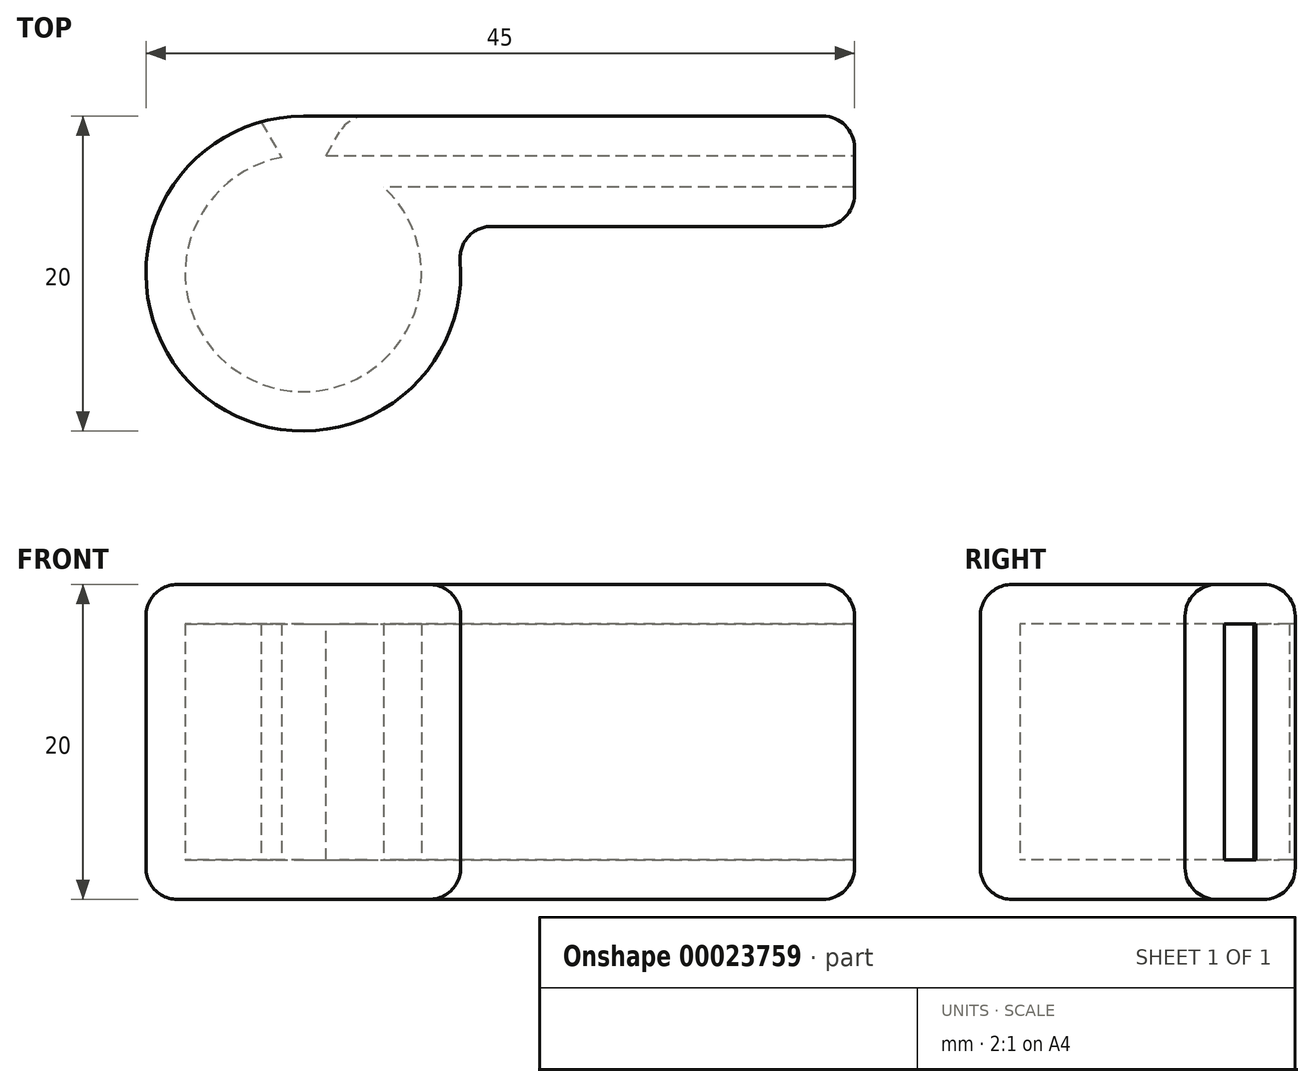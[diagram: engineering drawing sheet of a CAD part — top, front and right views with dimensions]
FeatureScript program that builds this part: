
annotation { "Feature Type Name" : "Feature", "Feature Type Description" : "" }
export const myFeature = defineFeature(function(context is Context, id is Id, definition is map)
    precondition{}
    {
        {
            var Q0;
            Q0=qCreatedBy(makeId("Top.planeOp"),FACE);
            var sketch = newSketch(context, id + "F0", { "sketchPlane" : qUnion([Q0])});
            skLineSegment(sketch, "E0.bottom", {"start": v(0, 15) * mm, "end": v(35, 15) * mm});
            skLineSegment(sketch, "E0.left", {"start": v(0, 15) * mm, "end": v(0, 15) * mm});
            skLineSegment(sketch, "E0.right", {"start": v(35, 15) * mm, "end": v(35, 8) * mm});
            skLineSegment(sketch, "E1", {"start": v(-4.65, 18.05) * mm, "end": v(0, 10) * mm});
            skLineSegment(sketch, "E2", {"start": v(0, 10) * mm, "end": v(4.65, 18.05) * mm});
            skLineSegment(sketch, "E3", {"start": v(4.65, 18.05) * mm, "end": v(-4.65, 18.05) * mm});
            skLineSegment(sketch, "E4", {"start": v(19.14, 8) * mm, "end": v(35, 8) * mm});
            skArc(sketch, "E5", {"start": v(0, 15) * mm, "mid": v(-5.92, -3.06) * mm, "end": v(9.54, 8) * mm});
            skLineSegment(sketch, "E6", {"start": v(0, 5) * mm, "end": v(0, 5) * mm});
            skLineSegment(sketch, "E7", {"start": v(19.14, 8) * mm, "end": v(19.14, 8) * mm});
            skLineSegment(sketch, "E8", {"start": v(19.14, 8) * mm, "end": v(9.54, 8) * mm});
            skSolve(sketch);
        }
        {
            var Q0;
            {var subQ1=sQuery(id+"F0.wireOp",EDGE,"6024d693-16a0-4090-80fd-58b5c811e278");var subQ5=sQuery(id+"F0.wireOp",EDGE,"E0.top");var subQ7=makeQuery(id+"F0.imprint","INTERSECT",VERTEX,{"derivedFrom":[subQ1,subQ5]});Q0=makeQuery(id+"F0.imprint","IMPRINT",FACE,{"disambiguationData":[TD([[makeQuery(id+"F0.imprint","IMPRINT",EDGE,{"disambiguationData":[TD([[subQ7,-1.0]])],"derivedFrom":subQ1}),1.0]])]});}
            var Q1;
            {var subQ5=sQuery(id+"F0.wireOp",EDGE,"E0.right");Q1=makeQuery(id+"F0.imprint","IMPRINT",FACE,{"disambiguationData":[TD([[makeQuery(id+"F0.imprint","IMPRINT",EDGE,{"derivedFrom":subQ5}),-1.0]])]});}
            var Q2;
            {var subQ3=sQuery(id+"F0.wireOp",EDGE,"E0.top");var subQ5=sQuery(id+"F0.wireOp",EDGE,"6024d693-16a0-4090-80fd-58b5c811e278");var subQ6=makeQuery(id+"F0.imprint","INTERSECT",VERTEX,{"derivedFrom":[subQ5,subQ3]});Q2=makeQuery(id+"F0.imprint","IMPRINT",FACE,{"disambiguationData":[TD([[makeQuery(id+"F0.imprint","IMPRINT",EDGE,{"disambiguationData":[TD([[subQ6,1.0]])],"derivedFrom":subQ5}),1.0]])]});}
            var Q3;
            {var subQ0=sQuery(id+"F0.wireOp",EDGE,"E1");var subQ1=sQuery(id+"F0.wireOp",EDGE,"6024d693-16a0-4090-80fd-58b5c811e278");var subQ2=makeQuery(id+"F0.imprint","INTERSECT",VERTEX,{"derivedFrom":[subQ1,subQ0]});Q3=makeQuery(id+"F0.imprint","IMPRINT",FACE,{"disambiguationData":[TD([[makeQuery(id+"F0.imprint","IMPRINT",EDGE,{"disambiguationData":[TD([[subQ2,1.0]])],"derivedFrom":subQ1}),1.0]])]});}
            var Q4;
            {var subQ0=sQuery(id+"F0.wireOp",EDGE,"E2");var subQ1=sQuery(id+"F0.wireOp",EDGE,"6024d693-16a0-4090-80fd-58b5c811e278");var subQ2=makeQuery(id+"F0.imprint","INTERSECT",VERTEX,{"derivedFrom":[subQ1,subQ0]});Q4=makeQuery(id+"F0.imprint","IMPRINT",FACE,{"disambiguationData":[TD([[makeQuery(id+"F0.imprint","IMPRINT",EDGE,{"disambiguationData":[TD([[subQ2,-1.0]])],"derivedFrom":subQ1}),1.0]])]});}
            var Q5;
            {var subQ0=sQuery(id+"F0.wireOp",EDGE,"E2");var subQ3=sQuery(id+"F0.wireOp",EDGE,"E0.bottom");var subQ4=makeQuery(id+"F0.imprint","INTERSECT",VERTEX,{"derivedFrom":[subQ3,subQ0]});Q5=makeQuery(id+"F0.imprint","IMPRINT",FACE,{"disambiguationData":[TD([[makeQuery(id+"F0.imprint","IMPRINT",EDGE,{"disambiguationData":[TD([[subQ4,1.0]])],"derivedFrom":subQ0}),1.0]])]});}
            extrude(context, id + "F1", {"entities" : qUnion([Q0, Q1, Q2, Q3, Q4, Q5]), "depth" : 20 * mm});
        }
        {
            var Q0;
            Q0=makeQuery(id+"F1.opExtrude","SWEPT_FACE",FACE,{"disambiguationData":[OSD([sQuery(id+"F0.wireOp",EDGE,"E0.right")])]});
            shell(context, id + "F2", {"entities" : qUnion([Q0]), "thickness" : 2.5 * mm});
        }
        {
            var Q0;
            {var subQ7=sQuery(id+"F0.wireOp",EDGE,"E3");Q0=makeQuery(id+"F0.imprint","IMPRINT",FACE,{"disambiguationData":[TD([[makeQuery(id+"F0.imprint","IMPRINT",EDGE,{"derivedFrom":subQ7}),1.0]])]});}
            var Q1;
            {var subQ0=sQuery(id+"F0.wireOp",EDGE,"E5");var subQ3=sQuery(id+"F0.wireOp",EDGE,"E0.bottom");var subQ4=makeQuery(id+"F0.imprint","INTERSECT",VERTEX,{"derivedFrom":[subQ3,subQ0]});Q1=makeQuery(id+"F0.imprint","IMPRINT",FACE,{"disambiguationData":[TD([[makeQuery(id+"F0.imprint","IMPRINT",EDGE,{"disambiguationData":[TD([[subQ4,-1.0]])],"derivedFrom":subQ3}),-1.0]])]});}
            var Q2;
            Q2=sQuery(id+"F0.wireOp",EDGE,"E2");
            var Q3;
            Q3=sQuery(id+"F0.wireOp",EDGE,"E1");
            var Q4;
            Q4=sQuery(id+"F0.wireOp",EDGE,"E3");
            extrude(context, id + "F3", {"entities" : qUnion([Q0, Q1]), "operationType" : NewBodyOperationType.REMOVE, "surfaceEntities" : qUnion([Q2, Q3, Q4]), "depth" : 17.5 * mm});
        }
        {
            var Q0;
            {var subQ0=sQuery(id+"F0.wireOp",EDGE,"E5");var subQ3=sQuery(id+"F0.wireOp",EDGE,"E0.bottom");var subQ4=makeQuery(id+"F0.imprint","INTERSECT",VERTEX,{"derivedFrom":[subQ3,subQ0]});Q0=makeQuery(id+"F0.imprint","IMPRINT",FACE,{"disambiguationData":[TD([[makeQuery(id+"F0.imprint","IMPRINT",EDGE,{"disambiguationData":[TD([[subQ4,-1.0]])],"derivedFrom":subQ3}),-1.0]])]});}
            extrude(context, id + "F4", {"entities" : qUnion([Q0]), "operationType" : NewBodyOperationType.ADD, "depth" : 2.5 * mm});
        }
        {
            var Q0;
            Q0=makeQuery(id+"F1.opExtrude","CAP_EDGE",EDGE,{"disambiguationData":[OSD([sQuery(id+"F0.wireOp",EDGE,"E0.bottom")])],"isStart":false});
            var Q1;
            {var subQ0=sQuery(id+"F0.wireOp",EDGE,"E0.bottom");Q1=makeQuery(id+"F4.boolean.opBoolean","MERGE",EDGE,{"derivedFrom":[makeQuery(id+"F1.opExtrude","CAP_EDGE",EDGE,{"disambiguationData":[OSD([subQ0])],"isStart":true}),makeQuery(id+"F4.opExtrude","CAP_EDGE",EDGE,{"disambiguationData":[OSD([subQ0])],"isStart":true})]});}
            var Q2;
            Q2=makeQuery(id+"F1.opExtrude","SWEPT_FACE",FACE,{"disambiguationData":[OSD([sQuery(id+"F0.wireOp",EDGE,"E4")])]});
            var Q3;
            Q3=makeQuery(id+"F3.boolean.opBoolean","INTERSECT",EDGE,{"derivedFrom":[makeQuery(id+"F1.opExtrude","SWEPT_FACE",FACE,{"disambiguationData":[OSD([sQuery(id+"F0.wireOp",EDGE,"E0.bottom")])]}),makeQuery(id+"F3.opExtrude","SWEPT_FACE",FACE,{"disambiguationData":[OSD([sQuery(id+"F0.wireOp",EDGE,"E2")])]})]});
            var Q4;
            Q4=makeQuery(id+"F1.opExtrude","SWEPT_EDGE",EDGE,{"disambiguationData":[OSD([sQuery(id+"F0.wireOp",EDGE,"E0.bottom"),sQuery(id+"F0.wireOp",EDGE,"E0.right")])]});
            var Q5;
            Q5=makeQuery(id+"F1.opExtrude","CAP_EDGE",EDGE,{"disambiguationData":[OSD([sQuery(id+"F0.wireOp",EDGE,"E0.right")])],"isStart":false});
            var Q6;
            Q6=makeQuery(id+"F1.opExtrude","CAP_EDGE",EDGE,{"disambiguationData":[OSD([sQuery(id+"F0.wireOp",EDGE,"E0.right")])],"isStart":true});
            fillet(context, id + "F5", {"entities" : qUnion([Q0, Q1, Q2, Q3, Q4, Q5, Q6]), "radius" : 2 * mm, "tangentPropagation" : true, "allowEdgeOverflow" : false});
        }
    });
